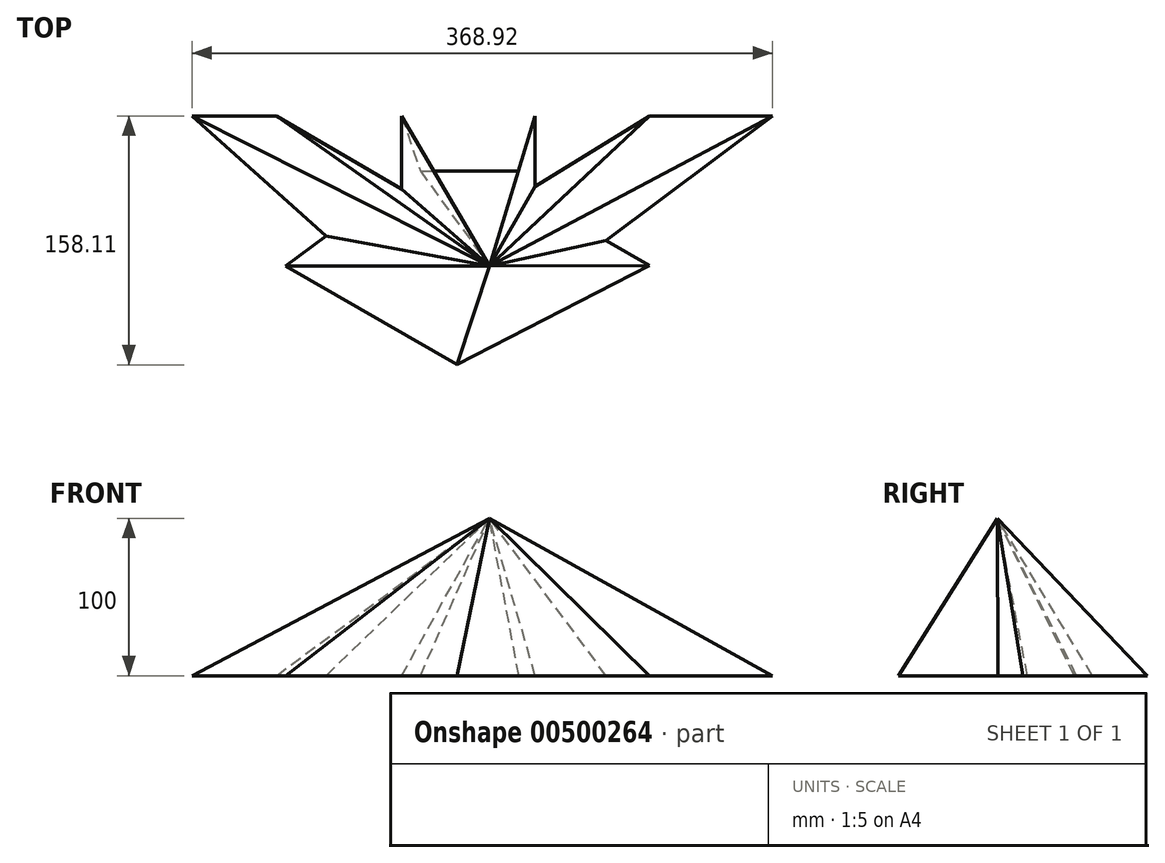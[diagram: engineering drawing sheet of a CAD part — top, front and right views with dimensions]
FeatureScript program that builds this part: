
annotation { "Feature Type Name" : "Feature", "Feature Type Description" : "" }
export const myFeature = defineFeature(function(context is Context, id is Id, definition is map)
    precondition{}
    {
        {
            var Q0;
            Q0=qCreatedBy(makeId("Top.planeOp"),FACE);
            var sketch = newSketch(context, id + "F0", { "sketchPlane" : qUnion([Q0])});
            skLineSegment(sketch, "E0", {"start": v(-55.74, 95.51) * mm, "end": v(-55.74, 48.92) * mm});
            skLineSegment(sketch, "E1", {"start": v(-55.74, 95.51) * mm, "end": v(-43.9, 60.38) * mm});
            skLineSegment(sketch, "E2", {"start": v(-43.9, 60.38) * mm, "end": v(18.74, 60.38) * mm});
            skLineSegment(sketch, "E3", {"start": v(18.74, 60.38) * mm, "end": v(29.05, 95.51) * mm});
            skLineSegment(sketch, "E4", {"start": v(29.05, 95.51) * mm, "end": v(29.05, 50.45) * mm});
            skLineSegment(sketch, "E5", {"start": v(29.05, 50.45) * mm, "end": v(101.6, 95.51) * mm});
            skLineSegment(sketch, "E6", {"start": v(-55.74, 48.92) * mm, "end": v(-135.17, 95.51) * mm});
            skLineSegment(sketch, "E7", {"start": v(-135.17, 95.51) * mm, "end": v(-189.02, 95.51) * mm});
            skLineSegment(sketch, "E8", {"start": v(101.6, 95.51) * mm, "end": v(179.9, 95.51) * mm});
            skLineSegment(sketch, "E9", {"start": v(-189.02, 95.51) * mm, "end": v(-103.8, 19.16) * mm});
            skLineSegment(sketch, "E10", {"start": v(179.9, 95.51) * mm, "end": v(74.11, 16.46) * mm});
            skLineSegment(sketch, "E11", {"start": v(-103.8, 19.16) * mm, "end": v(-129.44, 0) * mm});
            skLineSegment(sketch, "E12", {"start": v(74.11, 16.46) * mm, "end": v(101.6, 0.33) * mm});
            skLineSegment(sketch, "E13", {"start": v(-129.44, 0) * mm, "end": v(-20.6, -62.6) * mm});
            skLineSegment(sketch, "E14", {"start": v(101.6, 0.33) * mm, "end": v(-20.6, -62.6) * mm});
            skSolve(sketch);
        }
        {
            var Q0;
            Q0=qCreatedBy(makeId("Top.planeOp"),FACE);
            cPlane(context, id + "F1", {"entities" : qUnion([Q0]), "cplaneType" : CPlaneType.OFFSET, "offset" : 100 * mm, "width" : 150 * mm, "height" : 150 * mm});
        }
        {
            var Q0;
            Q0=qCreatedBy(id+"F1.planeOp",FACE);
            var sketch = newSketch(context, id + "F2", { "sketchPlane" : qUnion([Q0])});
            skPoint(sketch, "E15", {"position": v(0, 0) * mm});
            skSolve(sketch);
        }
        {
            var Q0;
            Q0=makeQuery(id+"F0.imprint","IMPRINT",FACE,{"disambiguationData":[TD([[makeQuery(id+"F0.imprint","IMPRINT",EDGE,{"derivedFrom":sQuery(id+"F0.wireOp",EDGE,"E0")}),1.0]])]});
            var Q1;
            Q1=sQuery(id+"F2.wireOp",VERTEX,"E15");
            loft(context, id + "F3", {"sheetProfilesArray" : [{ "sheetProfileEntities" : qUnion([Q0]) }, { "sheetProfileEntities" : qUnion([Q1]) }]});
        }
    });
